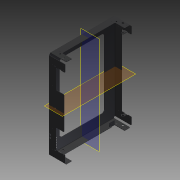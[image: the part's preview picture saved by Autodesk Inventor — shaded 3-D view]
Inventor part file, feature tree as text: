
AUTODESK INVENTOR PART (.ipt)
format: ipt  version: 2015 (Build 190159000, 159)  size: 1,107,456 bytes
history: native  units: mm
features: hole x17, extrude x16, fillet x9, projected_geometry x6, other x3, mirror x1, pattern_linear x1
ambient origin geometry x8: Origin, YZ Plane, XZ Plane, XY Plane, X Axis, Y Axis, Z Axis, Center Point
bodies: Solid1 (feature_tree)
feature tree (53):
  extrude  "Extrusión1"  Depth=2.0mm
  extrude  "Extrusión2"  Depth=2.0mm
  hole  "Agujero1"  [1 undecoded]
  extrude  "Extrusión3"  Depth=150.0mm
  extrude  "Extrusión4"  Depth=485.0mm TaperAngle=0.0deg
  fillet  "Empalme1"  Radius=60.0mm
  hole  "Agujero2"  [1 undecoded]
  hole  "Agujero3"  [1 undecoded]
  extrude  "Extrusión6"  Depth=2.0mm
  extrude  "Extrusión7"  Depth=2.0mm
  hole  "Agujero7"  [1 undecoded]
  extrude  "Extrusión9"  Depth=8.0mm
  hole  "Agujero8"  [1 undecoded]
  hole  "Agujero9"  [1 undecoded]
  hole  "Agujero10"  [1 undecoded]
  fillet  "Empalme3"  Radius=25.0mm
  hole  "Agujero12"  [1 undecoded]
  hole  "Agujero13"  [1 undecoded]
  hole  "Agujero14"  [1 undecoded]
  mirror  "Simetría2"
  extrude  "Extrusión10"  Depth=55.0mm
  hole  "Agujero15"  [1 undecoded]
  hole  "Agujero16"  [1 undecoded]
  hole  "aGUJEROS APOYO PTFE"  [1 undecoded]
  fillet  "Redondeo de esquina1"  Radius=40.0mm
  hole  "Agujero18"  [1 undecoded]
  extrude  "Extrusión12"  Depth=40.0mm
  other  "Desplazar cara2"
  extrude  "Extrusión13"  Depth=40.0mm
  fillet  "Empalme4"  Radius=40.0mm
  extrude  "Extrusión14"  Depth=112.0mm TaperAngle=0.0deg
  extrude  "Extrusión15"  Depth=61.0mm
  hole  "Agujero4 Ø10.1"  [1 undecoded]
  fillet  "Empalme7"  Radius=40.0mm
  extrude  "Extrusión16"  Depth=20.0mm
  extrude  "Extrusión17"  Depth=25.0mm
  hole  "Agujero19"  [1 undecoded]
  fillet  "Empalme8"  Radius=22.0mm
  other  "Desplazar cara3"
  fillet  "Empalme9"  Radius=10.5mm
  hole  "Agujero20"  [1 undecoded]
  extrude  "Extrusión19"  Depth=122.0mm
  fillet  "Redondeo de esquina2"  Radius=6.0mm
  extrude  "Extrusión20"  Depth=10.0mm TaperAngle=0.0deg
  pattern_linear  "Patrón rectangular2"  Count1=40  [1 undecoded]
  fillet  "Empalme6"  Radius=15.0mm
  projected_geometry  "Contorno proyectado4"
  projected_geometry  "Contorno proyectado5"
  projected_geometry  "Contorno proyectado6"
  projected_geometry  "Contorno proyectado7"
  projected_geometry  "Contorno proyectado8"
  projected_geometry  "Contorno proyectado9"
  other  "Definición1"
note: 18 required parameter values undecoded (feature->parameter linkage not recoverable at this tier; creation-order binding heuristic only, values carry confidence <= 0.55)
